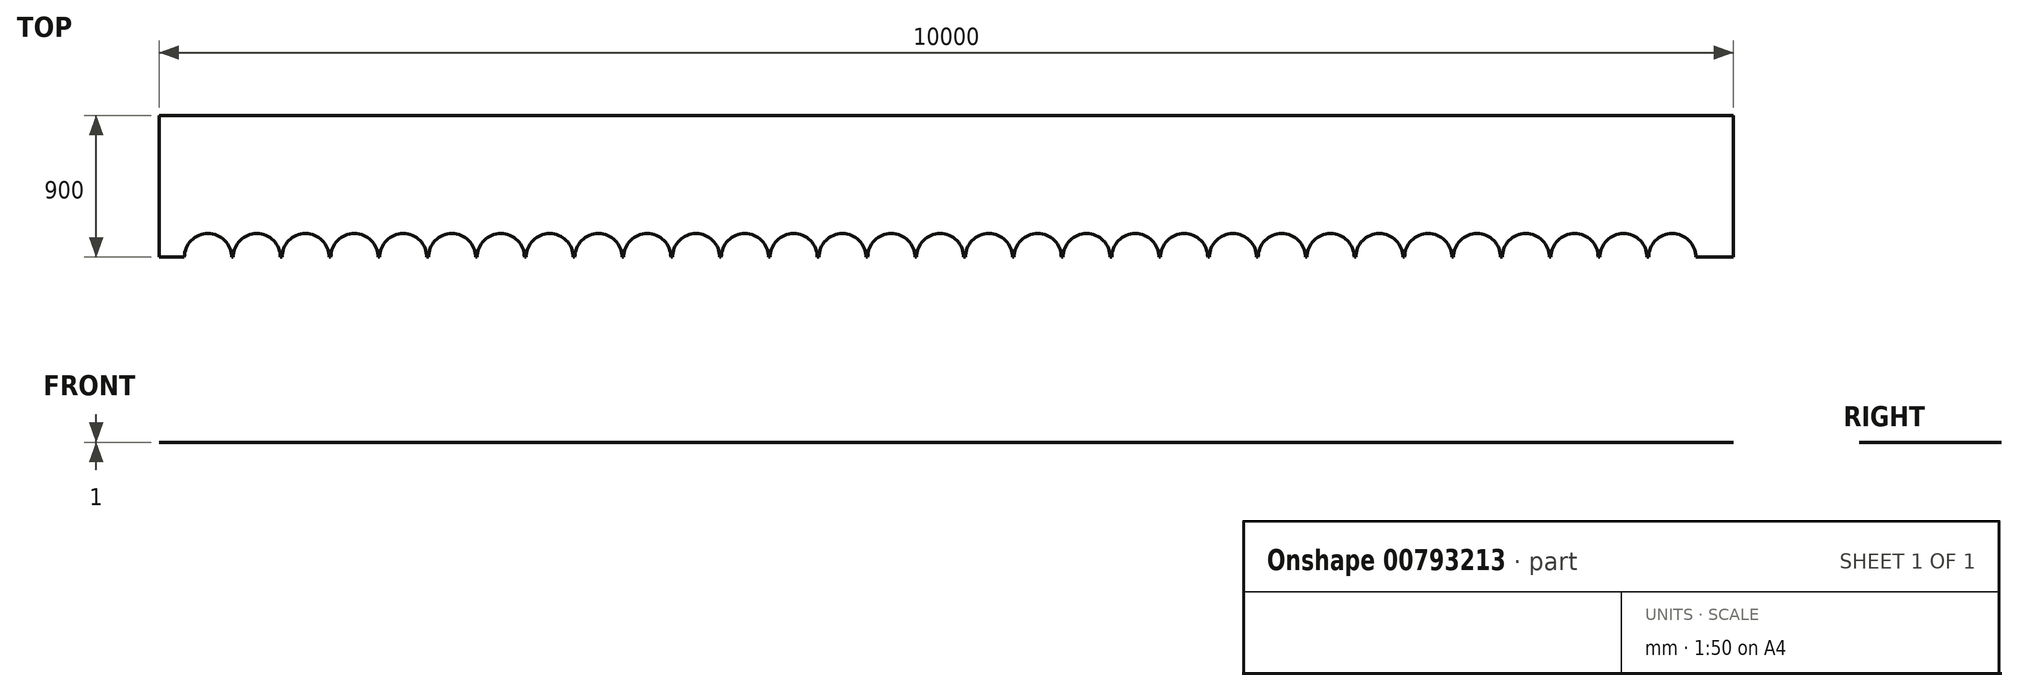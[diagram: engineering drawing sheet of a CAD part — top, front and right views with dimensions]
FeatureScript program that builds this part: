
annotation { "Feature Type Name" : "Feature", "Feature Type Description" : "" }
export const myFeature = defineFeature(function(context is Context, id is Id, definition is map)
    precondition{}
    {
        {
            var Q0;
            Q0=qCreatedBy(makeId("Top.planeOp"),FACE);
            var sketch = newSketch(context, id + "F0", { "sketchPlane" : qUnion([Q0])});
            skLineSegment(sketch, "E0.bottom", {"start": v(0, 0) * mm, "end": v(10000, 0) * mm});
            skLineSegment(sketch, "E0.top", {"start": v(0, -1800) * mm, "end": v(10000, -1800) * mm});
            skLineSegment(sketch, "E0.left", {"start": v(0, 0) * mm, "end": v(0, -1800) * mm});
            skLineSegment(sketch, "E0.right", {"start": v(10000, 0) * mm, "end": v(10000, -1800) * mm});
            skSolve(sketch);
        }
        {
            var Q0;
            Q0=makeQuery(id+"F0.imprint","IMPRINT",FACE,{"disambiguationData":[TD([[makeQuery(id+"F0.imprint","IMPRINT",EDGE,{"derivedFrom":sQuery(id+"F0.wireOp",EDGE,"E0.bottom")}),-1.0]])]});
            extrude(context, id + "F1", {"entities" : qUnion([Q0]), "depth" : 1 * mm, "offsetDistance" : 25 * mm});
        }
        {
            var Q0;
            Q0=makeQuery(id+"F1.opExtrude","CAP_FACE",FACE,{"disambiguationData":[OSD([sQuery(id+"F0.wireOp",EDGE,"E0.bottom"),sQuery(id+"F0.wireOp",EDGE,"E0.top"),sQuery(id+"F0.wireOp",EDGE,"E0.left"),sQuery(id+"F0.wireOp",EDGE,"E0.right")])],"isStart":false});
            var sketch = newSketch(context, id + "F2", { "sketchPlane" : qUnion([Q0])});
            skCircle(sketch, "E1", {"center": v(310.35, -900) * mm, "radius": 150 * mm});
            skPoint(sketch, "E1.centerSnap0", {"position": v(0, -900) * mm});
            skCircle(sketch, "E2.1.0.0", {"center": v(620.35, -900) * mm, "radius": 150 * mm});
            skCircle(sketch, "E2.2.0.0", {"center": v(930.35, -900) * mm, "radius": 150 * mm});
            skCircle(sketch, "E2.3.0.0", {"center": v(1240.35, -900) * mm, "radius": 150 * mm});
            skCircle(sketch, "E2.4.0.0", {"center": v(1550.35, -900) * mm, "radius": 150 * mm});
            skCircle(sketch, "E2.5.0.0", {"center": v(1860.35, -900) * mm, "radius": 150 * mm});
            skCircle(sketch, "E2.6.0.0", {"center": v(2170.35, -900) * mm, "radius": 150 * mm});
            skCircle(sketch, "E2.7.0.0", {"center": v(2480.35, -900) * mm, "radius": 150 * mm});
            skCircle(sketch, "E2.8.0.0", {"center": v(2790.35, -900) * mm, "radius": 150 * mm});
            skCircle(sketch, "E2.9.0.0", {"center": v(3100.35, -900) * mm, "radius": 150 * mm});
            skCircle(sketch, "E2.10.0.0", {"center": v(3410.35, -900) * mm, "radius": 150 * mm});
            skCircle(sketch, "E2.11.0.0", {"center": v(3720.35, -900) * mm, "radius": 150 * mm});
            skCircle(sketch, "E2.12.0.0", {"center": v(4030.35, -900) * mm, "radius": 150 * mm});
            skCircle(sketch, "E2.13.0.0", {"center": v(4340.35, -900) * mm, "radius": 150 * mm});
            skCircle(sketch, "E2.14.0.0", {"center": v(4650.35, -900) * mm, "radius": 150 * mm});
            skCircle(sketch, "E2.15.0.0", {"center": v(4960.35, -900) * mm, "radius": 150 * mm});
            skCircle(sketch, "E2.16.0.0", {"center": v(5270.35, -900) * mm, "radius": 150 * mm});
            skCircle(sketch, "E2.17.0.0", {"center": v(5580.35, -900) * mm, "radius": 150 * mm});
            skCircle(sketch, "E2.18.0.0", {"center": v(5890.35, -900) * mm, "radius": 150 * mm});
            skCircle(sketch, "E2.19.0.0", {"center": v(6200.35, -900) * mm, "radius": 150 * mm});
            skCircle(sketch, "E2.20.0.0", {"center": v(6510.35, -900) * mm, "radius": 150 * mm});
            skCircle(sketch, "E2.21.0.0", {"center": v(6820.35, -900) * mm, "radius": 150 * mm});
            skCircle(sketch, "E2.22.0.0", {"center": v(7130.35, -900) * mm, "radius": 150 * mm});
            skCircle(sketch, "E2.23.0.0", {"center": v(7440.35, -900) * mm, "radius": 150 * mm});
            skCircle(sketch, "E2.24.0.0", {"center": v(7750.35, -900) * mm, "radius": 150 * mm});
            skCircle(sketch, "E2.25.0.0", {"center": v(8060.35, -900) * mm, "radius": 150 * mm});
            skCircle(sketch, "E2.26.0.0", {"center": v(8370.35, -900) * mm, "radius": 150 * mm});
            skCircle(sketch, "E2.27.0.0", {"center": v(8680.35, -900) * mm, "radius": 150 * mm});
            skCircle(sketch, "E2.28.0.0", {"center": v(8990.35, -900) * mm, "radius": 150 * mm});
            skCircle(sketch, "E2.29.0.0", {"center": v(9300.35, -900) * mm, "radius": 150 * mm});
            skCircle(sketch, "E2.30.0.0", {"center": v(9610.35, -900) * mm, "radius": 150 * mm});
            skLineSegment(sketch, "E2.direction1", {"start": v(310.35, -900) * mm, "end": v(620.35, -900) * mm, "construction": true});
            skSolve(sketch);
        }
        {
            var Q0;
            Q0 = qSketchRegion(id + "F2", true);
            extrude(context, id + "F3", {"entities" : qUnion([Q0]), "operationType" : NewBodyOperationType.REMOVE, "endBound" : BoundingType.THROUGH_ALL, "oppositeDirection" : true, "depth" : 25 * mm, "offsetDistance" : 25 * mm});
        }
        {
            var Q0;
            Q0=makeQuery(id+"F1.opExtrude","CAP_FACE",FACE,{"disambiguationData":[OSD([sQuery(id+"F0.wireOp",EDGE,"E0.bottom"),sQuery(id+"F0.wireOp",EDGE,"E0.top"),sQuery(id+"F0.wireOp",EDGE,"E0.left"),sQuery(id+"F0.wireOp",EDGE,"E0.right")])],"isStart":false});
            var sketch = newSketch(context, id + "F4", { "sketchPlane" : qUnion([Q0])});
            skLineSegment(sketch, "E3", {"start": v(0, -900) * mm, "end": v(10000, -900) * mm});
            skSolve(sketch);
        }
        {
            var Q0;
            {var subQ35=makeQuery(id+"F1.opExtrude","CAP_EDGE",EDGE,{"disambiguationData":[OSD([sQuery(id+"F0.wireOp",EDGE,"E0.top")])],"isStart":false});Q0=makeQuery(id+"F4.imprint","IMPRINT",FACE,{"disambiguationData":[TD([[makeQuery(id+"F4.imprint","IMPRINT",EDGE,{"derivedFrom":subQ35}),1.0]])]});}
            extrude(context, id + "F5", {"entities" : qUnion([Q0]), "operationType" : NewBodyOperationType.REMOVE, "endBound" : BoundingType.THROUGH_ALL, "oppositeDirection" : true, "depth" : 25 * mm, "offsetDistance" : 25 * mm});
        }
    });
